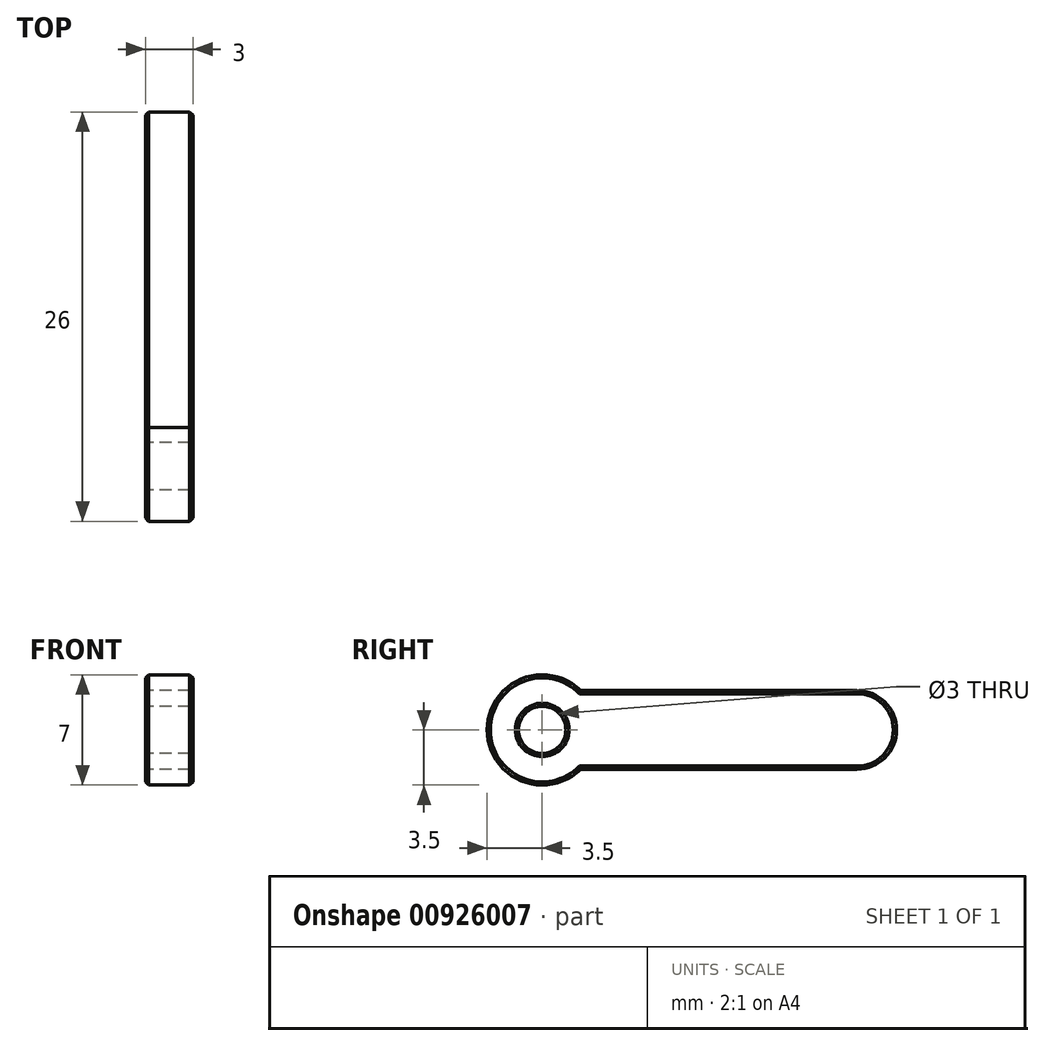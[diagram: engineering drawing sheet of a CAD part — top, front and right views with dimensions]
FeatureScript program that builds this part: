
annotation { "Feature Type Name" : "Feature", "Feature Type Description" : "" }
export const myFeature = defineFeature(function(context is Context, id is Id, definition is map)
    precondition{}
    {
        {
            var Q0;
            Q0=qCreatedBy(makeId("Right.planeOp"),FACE);
            var sketch = newSketch(context, id + "F0", { "sketchPlane" : qUnion([Q0])});
            skLineSegment(sketch, "E0.bottom", {"start": v(10, 2.5) * mm, "end": v(-7.55, 2.5) * mm});
            skLineSegment(sketch, "E0.top", {"start": v(10, -2.5) * mm, "end": v(-7.55, -2.5) * mm});
            skLineSegment(sketch, "E0.left", {"start": v(12.5, 0) * mm, "end": v(12.5, 0) * mm});
            skLineSegment(sketch, "E0.right", {"start": v(-12.5, 0) * mm, "end": v(-12.5, 0) * mm});
            skPoint(sketch, "E0.middle", {"position": v(0, 0) * mm});
            skLineSegment(sketch, "E1", {"start": v(-12.5, 0) * mm, "end": v(-10, 0) * mm});
            skCircle(sketch, "E2", {"center": v(-10, 0) * mm, "radius": 1.5 * mm});
            skPoint(sketch, "E3.visualSharp", {"position": v(-12.5, 2.5) * mm});
            skPoint(sketch, "E4.visualSharp", {"position": v(-12.5, -2.5) * mm});
            skPoint(sketch, "E5.visualSharp", {"position": v(12.5, 2.5) * mm});
            skArc(sketch, "E5.filletArc", {"start": v(12.5, 0) * mm, "mid": v(11.77, 1.77) * mm, "end": v(10, 2.5) * mm});
            skPoint(sketch, "E6.visualSharp", {"position": v(12.5, -2.5) * mm});
            skArc(sketch, "E6.filletArc", {"start": v(10, -2.5) * mm, "mid": v(11.77, -1.77) * mm, "end": v(12.5, 0) * mm});
            skArc(sketch, "E7", {"start": v(-7.55, 2.5) * mm, "mid": v(-13.5, 0) * mm, "end": v(-7.55, -2.5) * mm});
            skSolve(sketch);
        }
        {
            var Q0;
            Q0=makeQuery(id+"F0.imprint","IMPRINT",FACE,{"disambiguationData":[TD([[makeQuery(id+"F0.imprint","IMPRINT",EDGE,{"derivedFrom":sQuery(id+"F0.wireOp",EDGE,"E0.bottom")}),1.0]])]});
            extrude(context, id + "F1", {"entities" : qUnion([Q0]), "depth" : 3 * mm, "offsetDistance" : 25 * mm});
        }
        {
            var Q0;
            Q0=makeQuery(id+"F1.opExtrude","CAP_FACE",FACE,{"disambiguationData":[OSD([sQuery(id+"F0.wireOp",EDGE,"E0.bottom"),sQuery(id+"F0.wireOp",EDGE,"E0.top"),sQuery(id+"F0.wireOp",EDGE,"E2"),sQuery(id+"F0.wireOp",EDGE,"E3.filletArc"),sQuery(id+"F0.wireOp",EDGE,"E4.filletArc"),sQuery(id+"F0.wireOp",EDGE,"E5.filletArc"),sQuery(id+"F0.wireOp",EDGE,"E6.filletArc")])],"isStart":false});
            var Q1;
            Q1=makeQuery(id+"F1.opExtrude","CAP_FACE",FACE,{"disambiguationData":[OSD([sQuery(id+"F0.wireOp",EDGE,"E0.bottom"),sQuery(id+"F0.wireOp",EDGE,"E0.top"),sQuery(id+"F0.wireOp",EDGE,"E2"),sQuery(id+"F0.wireOp",EDGE,"E3.filletArc"),sQuery(id+"F0.wireOp",EDGE,"E4.filletArc"),sQuery(id+"F0.wireOp",EDGE,"E5.filletArc"),sQuery(id+"F0.wireOp",EDGE,"E6.filletArc")])],"isStart":true});
            chamfer(context, id + "F2", {"entities" : qUnion([Q0, Q1]), "width" : 0.2 * mm, "tangentPropagation" : true});
        }
    });
